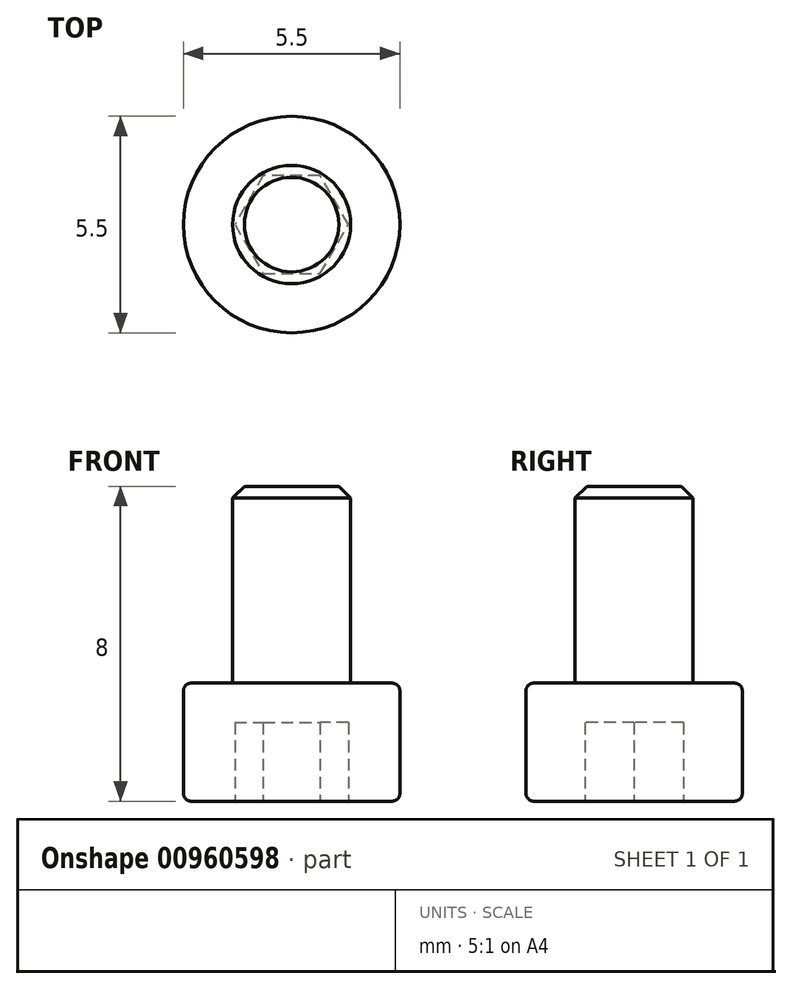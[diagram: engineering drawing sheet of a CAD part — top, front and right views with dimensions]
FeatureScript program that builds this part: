
annotation { "Feature Type Name" : "Feature", "Feature Type Description" : "" }
export const myFeature = defineFeature(function(context is Context, id is Id, definition is map)
    precondition{}
    {
        {
            var Q0;
            Q0=qCreatedBy(makeId("Front.planeOp"),FACE);
            var sketch = newSketch(context, id + "F0", { "sketchPlane" : qUnion([Q0])});
            skLineSegment(sketch, "E0", {"start": v(0, 0) * mm, "end": v(0, 8) * mm});
            skLineSegment(sketch, "E1", {"start": v(0, 8) * mm, "end": v(-1.5, 8) * mm});
            skLineSegment(sketch, "E2", {"start": v(-1.5, 8) * mm, "end": v(-1.5, 3) * mm});
            skLineSegment(sketch, "E3", {"start": v(-1.5, 3) * mm, "end": v(-2.75, 3) * mm});
            skLineSegment(sketch, "E4", {"start": v(-2.75, 3) * mm, "end": v(-2.75, 0) * mm});
            skLineSegment(sketch, "E5", {"start": v(-2.75, 0) * mm, "end": v(0, 0) * mm});
            skSolve(sketch);
        }
        {
            var Q0;
            Q0=makeQuery(id+"F0.imprint","IMPRINT",FACE,{"disambiguationData":[TD([[makeQuery(id+"F0.imprint","IMPRINT",EDGE,{"derivedFrom":sQuery(id+"F0.wireOp",EDGE,"E0")}),1.0]])]});
            var Q1;
            Q1=sQuery(id+"F0.wireOp",EDGE,"E0");
            revolve(context, id + "F1", {"surfaceOperationType" : NewSurfaceOperationType.NEW, "entities" : qUnion([Q0]), "axis" : qUnion([Q1]), "revolveType" : RevolveType.FULL});
        }
        {
            var Q0;
            Q0=makeQuery(id+"F1.opRevolve","SWEPT_FACE",FACE,{"disambiguationData":[OSD([sQuery(id+"F0.wireOp",EDGE,"E5")])]});
            var sketch = newSketch(context, id + "F2", { "sketchPlane" : qUnion([Q0])});
            skCircle(sketch, "E6.cCircle", {"center": v(0, 0) * mm, "radius": 1.25 * mm, "construction": true});
            skLineSegment(sketch, "E6.0", {"start": v(-0.72, 1.25) * mm, "end": v(0.72, 1.25) * mm});
            skLineSegment(sketch, "E6.1", {"start": v(0.72, 1.25) * mm, "end": v(1.44, 0) * mm});
            skLineSegment(sketch, "E6.2", {"start": v(1.44, 0) * mm, "end": v(0.72, -1.25) * mm});
            skLineSegment(sketch, "E6.3", {"start": v(0.72, -1.25) * mm, "end": v(-0.72, -1.25) * mm});
            skLineSegment(sketch, "E6.4", {"start": v(-0.72, -1.25) * mm, "end": v(-1.44, 0) * mm});
            skLineSegment(sketch, "E6.5", {"start": v(-1.44, 0) * mm, "end": v(-0.72, 1.25) * mm});
            skPoint(sketch, "E6.0.midPoint", {"position": v(0, 1.25) * mm});
            skSolve(sketch);
        }
        {
            var Q0;
            Q0=makeQuery(id+"F2.imprint","IMPRINT",FACE,{"disambiguationData":[TD([[makeQuery(id+"F2.imprint","IMPRINT",EDGE,{"derivedFrom":sQuery(id+"F2.wireOp",EDGE,"E6.0")}),-1.0]])]});
            extrude(context, id + "F3", {"entities" : qUnion([Q0]), "operationType" : NewBodyOperationType.REMOVE, "oppositeDirection" : true, "depth" : 2 * mm, "offsetDistance" : 25 * mm});
        }
        {
            var Q0;
            Q0=makeQuery(id+"F1.opRevolve","SWEPT_EDGE",EDGE,{"disambiguationData":[OSD([sQuery(id+"F0.wireOp",EDGE,"E4"),sQuery(id+"F0.wireOp",EDGE,"E5")])]});
            var Q1;
            Q1=makeQuery(id+"F1.opRevolve","SWEPT_EDGE",EDGE,{"disambiguationData":[OSD([sQuery(id+"F0.wireOp",EDGE,"E3"),sQuery(id+"F0.wireOp",EDGE,"E4")])]});
            fillet(context, id + "F4", {"entities" : qUnion([Q0, Q1]), "radius" : .2 * mm, "tangentPropagation" : true, "allowEdgeOverflow" : false});
        }
        {
            var Q0;
            Q0=makeQuery(id+"F1.opRevolve","SWEPT_EDGE",EDGE,{"disambiguationData":[OSD([sQuery(id+"F0.wireOp",EDGE,"E1"),sQuery(id+"F0.wireOp",EDGE,"E2")])]});
            chamfer(context, id + "F5", {"entities" : qUnion([Q0]), "width" : .3 * mm, "tangentPropagation" : true});
        }
    });
